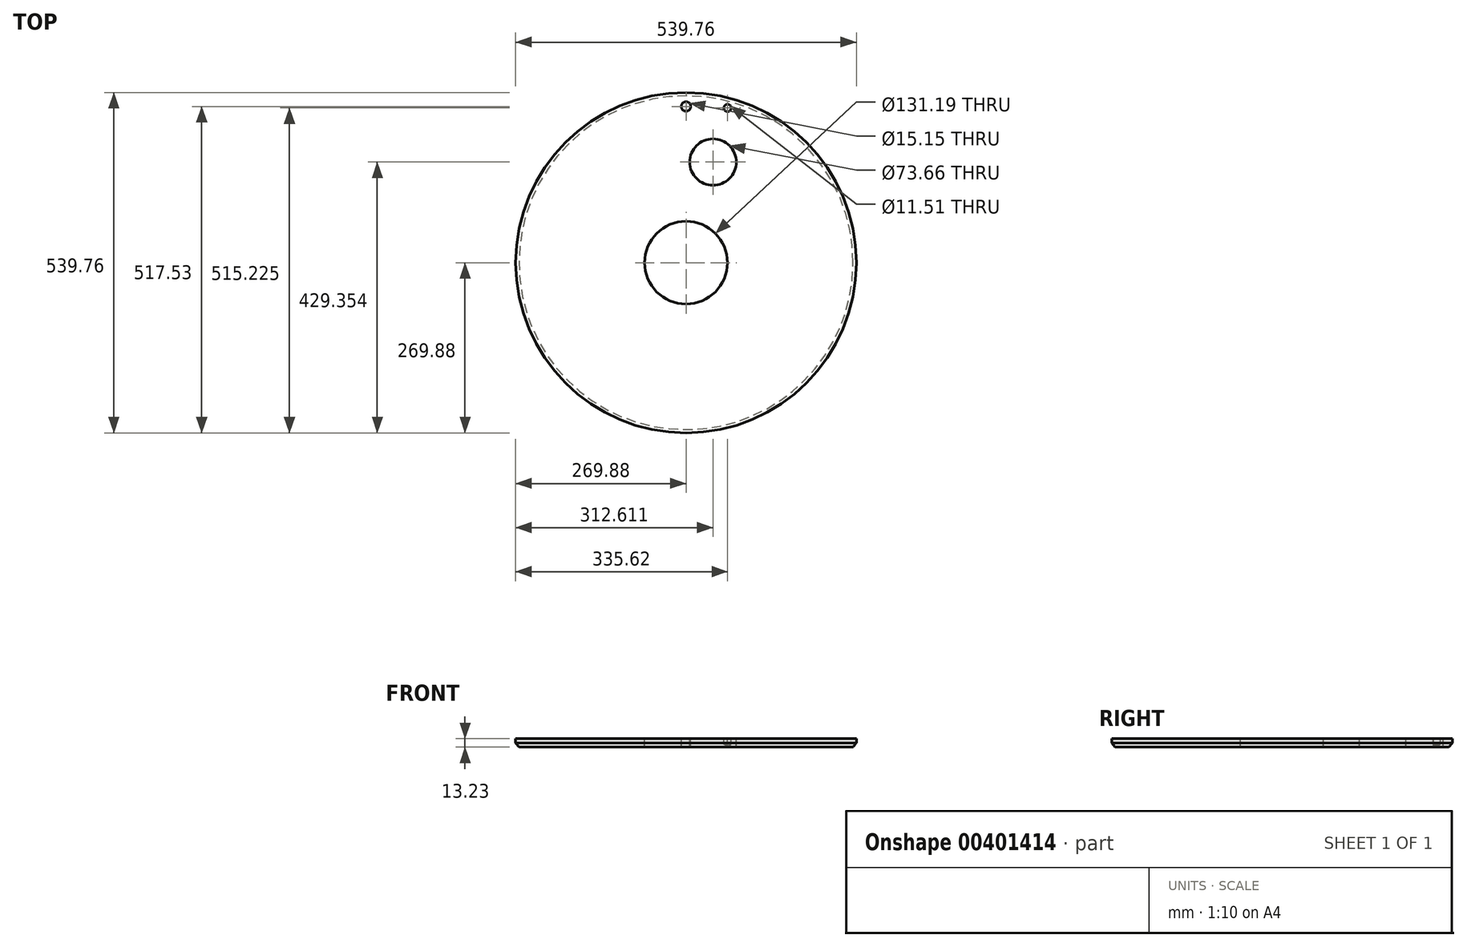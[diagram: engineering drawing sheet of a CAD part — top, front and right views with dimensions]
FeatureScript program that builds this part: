
annotation { "Feature Type Name" : "Feature", "Feature Type Description" : "" }
export const myFeature = defineFeature(function(context is Context, id is Id, definition is map)
    precondition{}
    {
        {
            var Q0;
            Q0=qCreatedBy(makeId("Top.planeOp"),FACE);
            var sketch = newSketch(context, id + "F0", { "sketchPlane" : qUnion([Q0])});
            skCircle(sketch, "E0", {"center": v(0, 0) * mm, "radius": 269.88 * mm});
            skCircle(sketch, "E1", {"center": v(0, 0) * mm, "radius": 65.6 * mm});
            skSolve(sketch);
        }
        {
            var Q0;
            Q0=makeQuery(id+"F0.imprint","IMPRINT",FACE,{"disambiguationData":[TD([[makeQuery(id+"F0.imprint","IMPRINT",EDGE,{"derivedFrom":sQuery(id+"F0.wireOp",EDGE,"E0")}),1.0]])]});
            extrude(context, id + "F1", {"entities" : qUnion([Q0]), "oppositeDirection" : true, "depth" : 13.23 * mm});
        }
        {
            var Q0;
            Q0=makeQuery(id+"F1.opExtrude","CAP_EDGE",EDGE,{"disambiguationData":[OSD([sQuery(id+"F0.wireOp",EDGE,"E0")])],"isStart":false});
            chamfer(context, id + "F2", {"entities" : qUnion([Q0]), "chamferType" : ChamferType.TWO_OFFSETS, "width1" : 6.8 * mm, "oppositeDirection" : false, "width2" : 5.23 * mm, "tangentPropagation" : true});
        }
        {
            var Q0;
            Q0=makeQuery(id+"F1.opExtrude","CAP_FACE",FACE,{"disambiguationData":[OSD([sQuery(id+"F0.wireOp",EDGE,"E0"),sQuery(id+"F0.wireOp",EDGE,"E1")])],"isStart":true});
            var sketch = newSketch(context, id + "F3", { "sketchPlane" : qUnion([Q0])});
            skCircle(sketch, "E2", {"center": v(0, 247.65) * mm, "radius": 7.58 * mm});
            skLineSegment(sketch, "E3", {"start": v(0, 87.22) * mm, "end": v(0, 0) * mm});
            skLineSegment(sketch, "E4", {"start": v(0, 0) * mm, "end": v(65.74, 245.35) * mm});
            skCircle(sketch, "E5", {"center": v(65.74, 245.35) * mm, "radius": 5.75 * mm});
            skSolve(sketch);
        }
        {
            var Q0;
            Q0=sQuery(id+"F3.wireOp",VERTEX,"E2.center");
            var Q1;
            Q1=makeQuery(id+"F1.opExtrude","SWEPT_BODY",BODY,{"disambiguationData":[OSD([sQuery(id+"F0.wireOp",EDGE,"E0"),sQuery(id+"F0.wireOp",EDGE,"E1")])]});
            hole(context, id + "F4", {"style" : HoleStyle.SIMPLE, "endStyle" : HoleEndStyle.THROUGH, "holeDiameter" : 15.15 * mm, "isTappedThrough" : true, "tappedDepth" : 12.7 * mm, "tapClearance" : 3, "locations" : qUnion([Q0]), "scope" : qUnion([Q1])});
        }
        {
            var Q0;
            Q0=qCreatedBy(makeId("Right.planeOp"),FACE);
            var sketch = newSketch(context, id + "F5", { "sketchPlane" : qUnion([Q0])});
            skLineSegment(sketch, "E6", {"start": v(0, 62.23) * mm, "end": v(0, -45.43) * mm});
            skSolve(sketch);
        }
        {
            var Q0;
            Q0=makeQuery(id+"F3.imprint","IMPRINT",FACE,{"disambiguationData":[TD([[makeQuery(id+"F3.imprint","IMPRINT",EDGE,{"derivedFrom":sQuery(id+"F3.wireOp",EDGE,"E2")}),-1.0]])]});
            var sketch = newSketch(context, id + "F6", { "sketchPlane" : qUnion([Q0])});
            skLineSegment(sketch, "E7", {"start": v(0, 75.07) * mm, "end": v(0, -48.17) * mm});
            skLineSegment(sketch, "E8", {"start": v(0, 0) * mm, "end": v(56.51, 210.91) * mm});
            skCircle(sketch, "E9", {"center": v(42.73, 159.47) * mm, "radius": 76.2 * mm});
            skSolve(sketch);
        }
        {
            var Q0;
            Q0=sQuery(id+"F6.wireOp",VERTEX,"E9.center");
            var Q1;
            Q1=makeQuery(id+"F1.opExtrude","SWEPT_BODY",BODY,{"disambiguationData":[OSD([sQuery(id+"F0.wireOp",EDGE,"E0"),sQuery(id+"F0.wireOp",EDGE,"E1")])]});
            hole(context, id + "F7", {"style" : HoleStyle.SIMPLE, "endStyle" : HoleEndStyle.THROUGH, "holeDiameter" : 73.66 * mm, "isTappedThrough" : true, "tappedDepth" : 12.7 * mm, "tapClearance" : 3, "locations" : qUnion([Q0]), "scope" : qUnion([Q1])});
        }
        {
            var Q0;
            Q0=sQuery(id+"F3.wireOp",VERTEX,"E5.center");
            var Q1;
            Q1=makeQuery(id+"F1.opExtrude","SWEPT_BODY",BODY,{"disambiguationData":[OSD([sQuery(id+"F0.wireOp",EDGE,"E0"),sQuery(id+"F0.wireOp",EDGE,"E1")])]});
            hole(context, id + "F8", {"style" : HoleStyle.SIMPLE, "endStyle" : HoleEndStyle.BLIND, "holeDiameter" : 11.5 * mm, "holeDepth" : 8.46 * mm, "isTappedThrough" : true, "tappedDepth" : 12.7 * mm, "tapClearance" : 3, "startFromSketch" : true, "locations" : qUnion([Q0]), "scope" : qUnion([Q1])});
        }
    });
